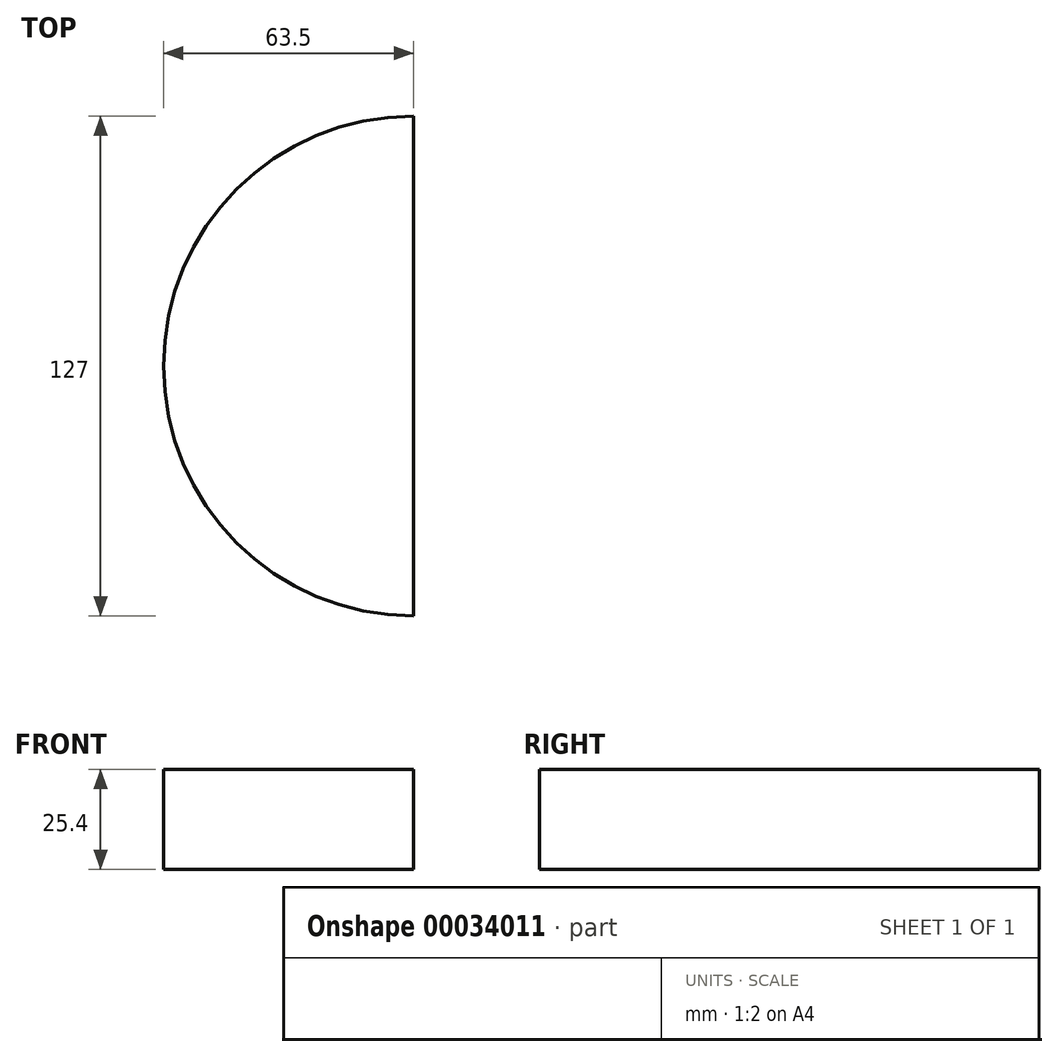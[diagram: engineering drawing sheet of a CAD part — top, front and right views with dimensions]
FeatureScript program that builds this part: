
annotation { "Feature Type Name" : "Feature", "Feature Type Description" : "" }
export const myFeature = defineFeature(function(context is Context, id is Id, definition is map)
    precondition{}
    {
        {
            var Q0;
            Q0=qCreatedBy(makeId("Top.planeOp"),FACE);
            var sketch = newSketch(context, id + "F0", { "sketchPlane" : qUnion([Q0])});
            skCircle(sketch, "E0", {"center": v(0, 0) * mm, "radius": 63.5 * mm});
            skLineSegment(sketch, "E1", {"start": v(0, 63.5) * mm, "end": v(0, -64.93) * mm});
            skSolve(sketch);
        }
        {
            var Q0;
            {var subQ0=sQuery(id+"F0.wireOp",EDGE,"E1");var subQ1=sQuery(id+"F0.wireOp",EDGE,"E0");var subQ3=makeQuery(id+"F0.imprint","INTERSECT",VERTEX,{"disambiguationData":[OD(0.0)],"derivedFrom":[subQ1,subQ0]});Q0=makeQuery(id+"F0.imprint","IMPRINT",FACE,{"disambiguationData":[TD([[makeQuery(id+"F0.imprint","IMPRINT",EDGE,{"disambiguationData":[TD([[subQ3,1.0]])],"derivedFrom":subQ1}),1.0]])]});}
            extrude(context, id + "F1", {"entities" : qUnion([Q0]), "depth" : 25.4 * mm});
        }
    });
